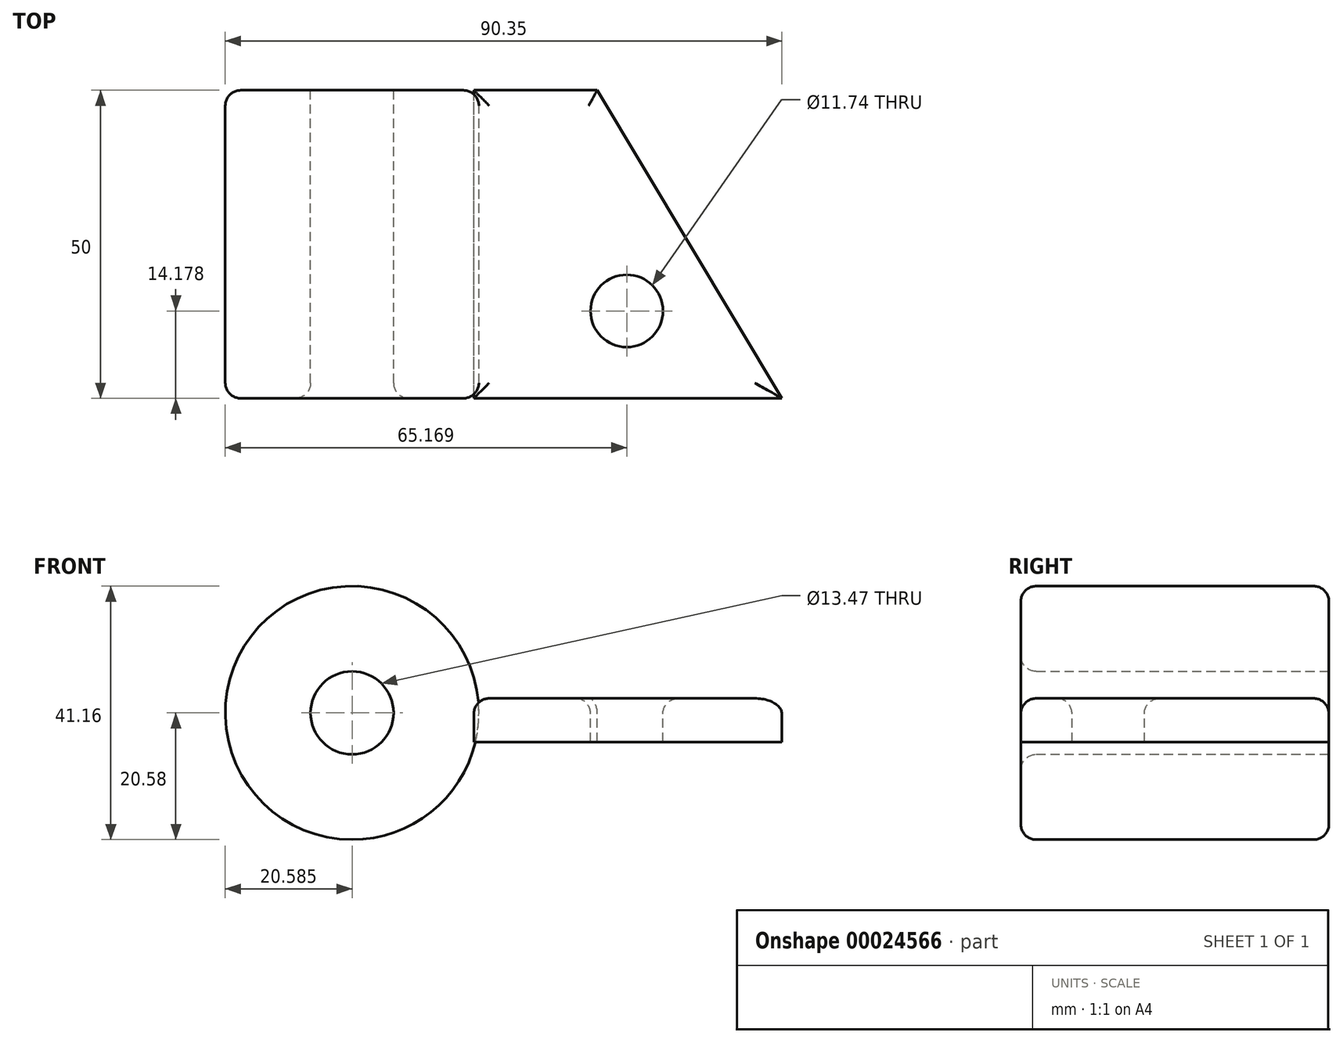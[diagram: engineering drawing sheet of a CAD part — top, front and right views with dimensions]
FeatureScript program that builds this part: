
annotation { "Feature Type Name" : "Feature", "Feature Type Description" : "" }
export const myFeature = defineFeature(function(context is Context, id is Id, definition is map)
    precondition{}
    {
        {
            var Q0;
            Q0=qCreatedBy(makeId("Front.planeOp"),FACE);
            var sketch = newSketch(context, id + "F0", { "sketchPlane" : qUnion([Q0])});
            skCircle(sketch, "E0", {"center": v(-44.76, 6.82) * mm, "radius": 20.58 * mm});
            skCircle(sketch, "E1", {"center": v(-44.76, 6.82) * mm, "radius": 6.74 * mm});
            skSolve(sketch);
        }
        {
            var Q0;
            Q0=makeQuery(id+"F0.imprint","IMPRINT",FACE,{"disambiguationData":[TD([[makeQuery(id+"F0.imprint","IMPRINT",EDGE,{"derivedFrom":sQuery(id+"F0.wireOp",EDGE,"E0")}),1.0]])]});
            extrude(context, id + "F1", {"entities" : qUnion([Q0]), "depth" : 50 * mm});
        }
        {
            var Q0;
            Q0=qCreatedBy(makeId("Right.planeOp"),FACE);
            var sketch = newSketch(context, id + "F2", { "sketchPlane" : qUnion([Q0])});
            skLineSegment(sketch, "E2.bottom", {"start": v(-50.14, 9.18) * mm, "end": v(0, 9.18) * mm});
            skLineSegment(sketch, "E2.top", {"start": v(-50.14, 2.1) * mm, "end": v(0, 2.1) * mm});
            skLineSegment(sketch, "E2.left", {"start": v(-50.14, 9.18) * mm, "end": v(-50.14, 2.1) * mm});
            skLineSegment(sketch, "E2.right", {"start": v(0, 9.18) * mm, "end": v(0, 2.1) * mm});
            skSolve(sketch);
        }
        {
            var Q0;
            Q0=makeQuery(id+"F2.imprint","IMPRINT",FACE,{"disambiguationData":[TD([[makeQuery(id+"F2.imprint","IMPRINT",EDGE,{"derivedFrom":sQuery(id+"F2.wireOp",EDGE,"E2.bottom")}),-1.0]])]});
            extrude(context, id + "F3", {"entities" : qUnion([Q0]), "oppositeDirection" : true, "depth" : 25 * mm});
        }
        {
            var Q0;
            Q0=makeQuery(id+"F3.opExtrude","CAP_FACE",FACE,{"disambiguationData":[OSD([sQuery(id+"F2.wireOp",EDGE,"E2.bottom"),sQuery(id+"F2.wireOp",EDGE,"E2.top"),sQuery(id+"F2.wireOp",EDGE,"E2.left"),sQuery(id+"F2.wireOp",EDGE,"E2.right")])],"isStart":true});
            extrude(context, id + "F4", {"entities" : qUnion([Q0]), "operationType" : NewBodyOperationType.ADD, "depth" : 25 * mm});
        }
        {
            var Q0;
            {var subQ0=sQuery(id+"F2.wireOp",EDGE,"E2.left");Q0=makeQuery(id+"F4.boolean.opBoolean","MERGE",FACE,{"derivedFrom":[makeQuery(id+"F3.opExtrude","SWEPT_FACE",FACE,{"disambiguationData":[OSD([subQ0])]}),makeQuery(id+"F4.opExtrude","SWEPT_FACE",FACE,{"disambiguationData":[OSD([subQ0])]})]});}
            var Q1;
            Q1=makeQuery(id+"F1.opExtrude","CAP_FACE",FACE,{"disambiguationData":[OSD([sQuery(id+"F0.wireOp",EDGE,"E0"),sQuery(id+"F0.wireOp",EDGE,"E1")])],"isStart":false});
            extrude(context, id + "F5", {"entities" : qUnion([Q0]), "operationType" : NewBodyOperationType.REMOVE, "endBound" : BoundingType.UP_TO_SURFACE, "oppositeDirection" : true, "endBoundEntityFace" : qUnion([Q1]), "depth" : 25 * mm});
        }
        {
            var Q0;
            {var subQ0=sQuery(id+"F2.wireOp",EDGE,"E2.bottom");Q0=makeQuery(id+"F4.boolean.opBoolean","MERGE",FACE,{"derivedFrom":[makeQuery(id+"F3.opExtrude","SWEPT_FACE",FACE,{"disambiguationData":[OSD([subQ0])]}),makeQuery(id+"F4.opExtrude","SWEPT_FACE",FACE,{"disambiguationData":[OSD([subQ0])]})]});}
            var sketch = newSketch(context, id + "F6", { "sketchPlane" : qUnion([Q0])});
            skLineSegment(sketch, "E3", {"start": v(25, -50) * mm, "end": v(-4.96, 0) * mm});
            skSolve(sketch);
        }
        {
            var Q0;
            {var subQ3=sQuery(id+"F6.wireOp",EDGE,"E3");Q0=makeQuery(id+"F6.imprint","IMPRINT",FACE,{"disambiguationData":[TD([[makeQuery(id+"F6.imprint","IMPRINT",EDGE,{"derivedFrom":subQ3}),-1.0]])]});}
            extrude(context, id + "F7", {"entities" : qUnion([Q0]), "operationType" : NewBodyOperationType.REMOVE, "endBound" : BoundingType.THROUGH_ALL, "oppositeDirection" : true, "depth" : 25 * mm});
        }
        {
            var Q0;
            {var subQ0=sQuery(id+"F2.wireOp",EDGE,"E2.bottom");Q0=makeQuery(id+"F4.boolean.opBoolean","MERGE",FACE,{"derivedFrom":[makeQuery(id+"F3.opExtrude","SWEPT_FACE",FACE,{"disambiguationData":[OSD([subQ0])]}),makeQuery(id+"F4.opExtrude","SWEPT_FACE",FACE,{"disambiguationData":[OSD([subQ0])]})]});}
            var sketch = newSketch(context, id + "F8", { "sketchPlane" : qUnion([Q0])});
            skCircle(sketch, "E4", {"center": v(-0.18, -35.82) * mm, "radius": 5.87 * mm});
            skSolve(sketch);
        }
        {
            var Q0;
            Q0=makeQuery(id+"F8.imprint","IMPRINT",FACE,{"disambiguationData":[TD([[makeQuery(id+"F8.imprint","IMPRINT",EDGE,{"derivedFrom":sQuery(id+"F8.wireOp",EDGE,"E4")}),1.0]])]});
            extrude(context, id + "F9", {"entities" : qUnion([Q0]), "operationType" : NewBodyOperationType.REMOVE, "endBound" : BoundingType.THROUGH_ALL, "oppositeDirection" : true, "depth" : 25 * mm});
        }
        {
            var Q0;
            Q0=makeQuery(id+"F5.boolean.opBoolean","MERGE",FACE,{"derivedFrom":[makeQuery(id+"F1.opExtrude","CAP_FACE",FACE,{"disambiguationData":[OSD([sQuery(id+"F0.wireOp",EDGE,"E0"),sQuery(id+"F0.wireOp",EDGE,"E1")])],"isStart":false}),makeQuery(id+"F5.opExtrude","CAP_FACE",FACE,{"disambiguationData":[OSD([sQuery(id+"F2.wireOp",EDGE,"E2.left")])],"isStart":false})]});
            var Q1;
            Q1=makeQuery(id+"F1.opExtrude","SWEPT_FACE",FACE,{"disambiguationData":[OSD([sQuery(id+"F0.wireOp",EDGE,"E0")])]});
            var Q2;
            {var subQ0=sQuery(id+"F2.wireOp",EDGE,"E2.bottom");Q2=makeQuery(id+"F4.boolean.opBoolean","MERGE",FACE,{"derivedFrom":[makeQuery(id+"F3.opExtrude","SWEPT_FACE",FACE,{"disambiguationData":[OSD([subQ0])]}),makeQuery(id+"F4.opExtrude","SWEPT_FACE",FACE,{"disambiguationData":[OSD([subQ0])]})]});}
            fillet(context, id + "F10", {"entities" : qUnion([Q0, Q1, Q2]), "radius" : 2.5 * mm, "tangentPropagation" : true, "allowEdgeOverflow" : false});
        }
    });
